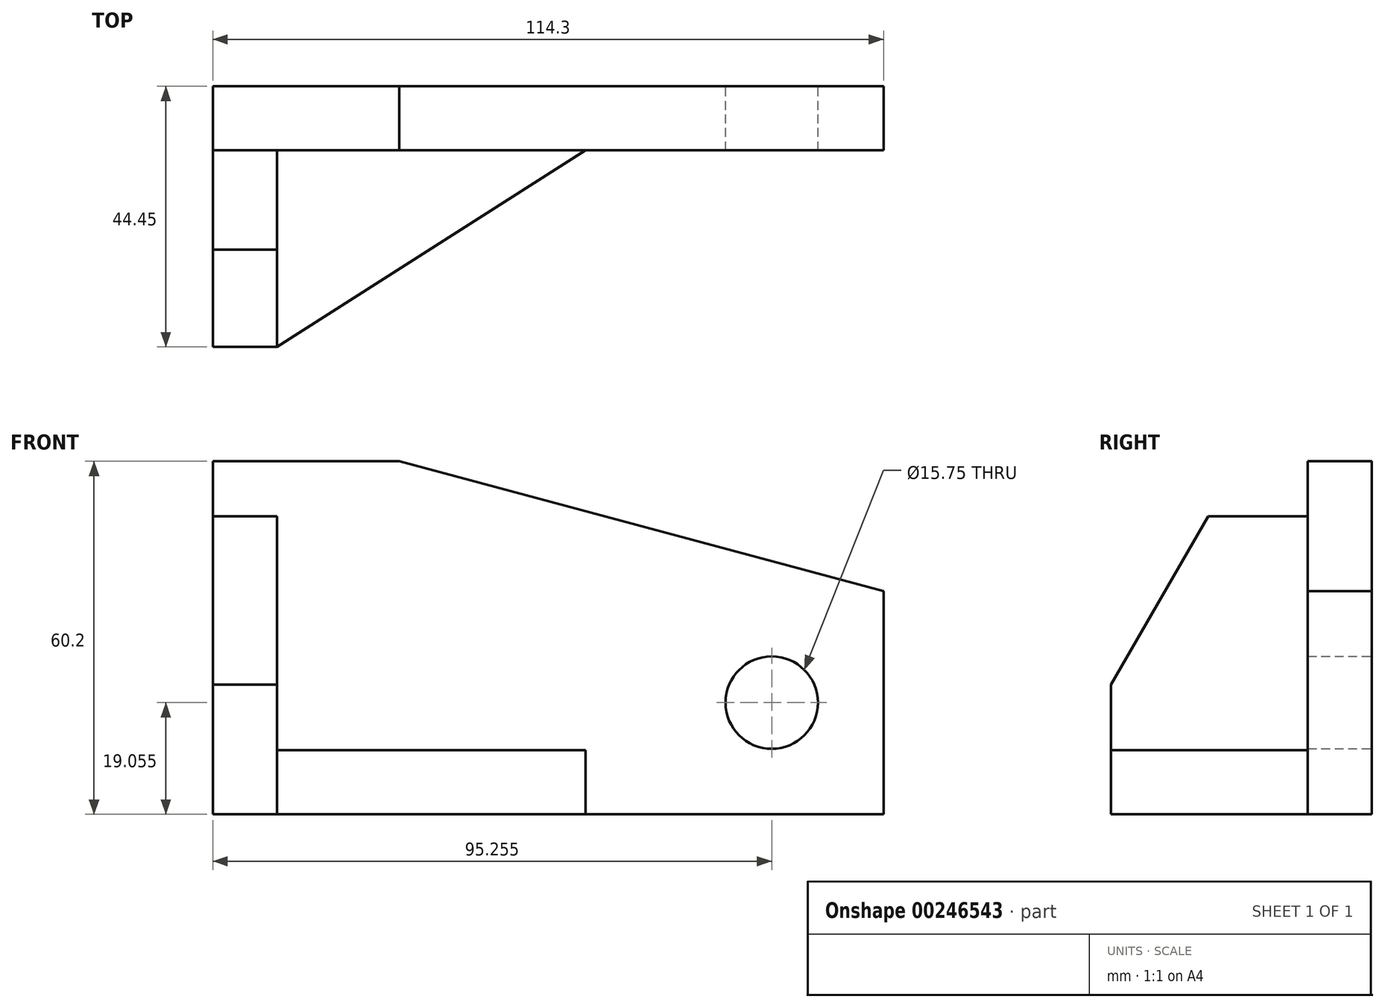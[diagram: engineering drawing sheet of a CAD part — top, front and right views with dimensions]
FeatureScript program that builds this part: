
annotation { "Feature Type Name" : "Feature", "Feature Type Description" : "" }
export const myFeature = defineFeature(function(context is Context, id is Id, definition is map)
    precondition{}
    {
        {
            var Q0;
            Q0=qCreatedBy(makeId("Front.planeOp"),FACE);
            var sketch = newSketch(context, id + "F0", { "sketchPlane" : qUnion([Q0])});
            skLineSegment(sketch, "E0.bottom", {"start": v(-52.56, 3.88) * mm, "end": v(-20.8, 3.88) * mm});
            skLineSegment(sketch, "E0.top", {"start": v(-52.56, -56.32) * mm, "end": v(61.74, -56.32) * mm});
            skLineSegment(sketch, "E0.left", {"start": v(-52.56, 3.88) * mm, "end": v(-52.56, -56.32) * mm});
            skLineSegment(sketch, "E0.right", {"start": v(61.74, -18.24) * mm, "end": v(61.74, -56.32) * mm});
            skLineSegment(sketch, "E1", {"start": v(-20.8, 3.88) * mm, "end": v(61.74, -18.24) * mm});
            skCircle(sketch, "E2", {"center": v(42.7, -37.27) * mm, "radius": 7.87 * mm});
            skSolve(sketch);
        }
        {
            var Q0;
            Q0=makeQuery(id+"F0.imprint","IMPRINT",FACE,{"disambiguationData":[TD([[makeQuery(id+"F0.imprint","IMPRINT",EDGE,{"derivedFrom":sQuery(id+"F0.wireOp",EDGE,"E0.top")}),1.0]])]});
            extrude(context, id + "F1", {"entities" : qUnion([Q0]), "depth" : 10.92 * mm});
        }
        {
            var Q0;
            Q0=makeQuery(id+"F1.opExtrude","CAP_FACE",FACE,{"disambiguationData":[OSD([sQuery(id+"F0.wireOp",EDGE,"E0.top"),sQuery(id+"F0.wireOp",EDGE,"E0.left"),sQuery(id+"F0.wireOp",EDGE,"E0.right"),sQuery(id+"F0.wireOp",EDGE,"E0.bottom"),sQuery(id+"F0.wireOp",EDGE,"E1"),sQuery(id+"F0.wireOp",EDGE,"E2")])],"isStart":false});
            var sketch = newSketch(context, id + "F2", { "sketchPlane" : qUnion([Q0])});
            skLineSegment(sketch, "E3", {"start": v(-52.56, -56.32) * mm, "end": v(-52.56, -5.52) * mm});
            skLineSegment(sketch, "E4", {"start": v(-52.56, -5.52) * mm, "end": v(-41.63, -5.52) * mm});
            skLineSegment(sketch, "E5", {"start": v(-41.63, -5.52) * mm, "end": v(-41.63, -56.32) * mm});
            skSolve(sketch);
        }
        {
            var Q0;
            {var subQ0=sQuery(id+"F2.wireOp",EDGE,"E3");Q0=makeQuery(id+"F2.imprint","IMPRINT",FACE,{"disambiguationData":[TD([[makeQuery(id+"F2.imprint","IMPRINT",EDGE,{"derivedFrom":subQ0}),1.0]])]});}
            extrude(context, id + "F3", {"entities" : qUnion([Q0]), "operationType" : NewBodyOperationType.ADD, "depth" : 33.53 * mm});
        }
        {
            var Q0;
            Q0=makeQuery(id+"F3.opExtrude","SWEPT_FACE",FACE,{"disambiguationData":[OSD([sQuery(id+"F2.wireOp",EDGE,"E5")])]});
            var sketch = newSketch(context, id + "F4", { "sketchPlane" : qUnion([Q0])});
            skLineSegment(sketch, "E6", {"start": v(-44.45, -56.32) * mm, "end": v(-44.45, -34.22) * mm});
            skLineSegment(sketch, "E7", {"start": v(-44.45, -34.22) * mm, "end": v(-27.88, -5.52) * mm});
            skLineSegment(sketch, "E8", {"start": v(-44.45, -56.32) * mm, "end": v(-44.45, -45.4) * mm});
            skLineSegment(sketch, "E9", {"start": v(-44.45, -45.4) * mm, "end": v(-10.92, -45.4) * mm});
            skLineSegment(sketch, "E10", {"start": v(-44.45, -34.22) * mm, "end": v(-44.45, -5.52) * mm});
            skLineSegment(sketch, "E11", {"start": v(-27.88, -5.52) * mm, "end": v(-10.92, -5.52) * mm});
            skSolve(sketch);
        }
        {
            var Q0;
            {var subQ0=sQuery(id+"F4.wireOp",EDGE,"E7");Q0=makeQuery(id+"F4.imprint","IMPRINT",FACE,{"disambiguationData":[TD([[makeQuery(id+"F4.imprint","IMPRINT",EDGE,{"derivedFrom":subQ0}),1.0]])]});}
            extrude(context, id + "F5", {"entities" : qUnion([Q0]), "operationType" : NewBodyOperationType.REMOVE, "oppositeDirection" : true, "depth" : 25.4 * mm});
        }
        {
            var Q0;
            Q0=makeQuery(id+"F3.opExtrude","SWEPT_FACE",FACE,{"disambiguationData":[OSD([sQuery(id+"F2.wireOp",EDGE,"E5")])]});
            var sketch = newSketch(context, id + "F6", { "sketchPlane" : qUnion([Q0])});
            skLineSegment(sketch, "E12", {"start": v(-44.45, -56.32) * mm, "end": v(-44.45, -45.4) * mm});
            skLineSegment(sketch, "E13", {"start": v(-44.45, -45.4) * mm, "end": v(-10.92, -45.4) * mm});
            skSolve(sketch);
        }
        {
            var Q0;
            Q0 = qSketchRegion(id + "F6", true);
            var Q1;
            Q1=makeQuery(id+"F6.imprint","IMPRINT",FACE,{"disambiguationData":[TD([[makeQuery(id+"F6.imprint","IMPRINT",EDGE,{"derivedFrom":sQuery(id+"F6.wireOp",EDGE,"E12")}),1.0]])]});
            extrude(context, id + "F7", {"entities" : qUnion([Q0, Q1]), "operationType" : NewBodyOperationType.ADD, "depth" : 52.58 * mm});
        }
        {
            var Q0;
            Q0=makeQuery(id+"F7.opExtrude","SWEPT_FACE",FACE,{"disambiguationData":[OSD([sQuery(id+"F6.wireOp",EDGE,"E13")])]});
            var sketch = newSketch(context, id + "F8", { "sketchPlane" : qUnion([Q0])});
            skLineSegment(sketch, "E14", {"start": v(-41.63, -44.45) * mm, "end": v(10.94, -10.92) * mm});
            skSolve(sketch);
        }
        {
            var Q0;
            Q0 = qSketchRegion(id + "F8", true);
            var Q1;
            Q1=makeQuery(id+"F8.imprint","IMPRINT",FACE,{"disambiguationData":[TD([[makeQuery(id+"F8.imprint","IMPRINT",EDGE,{"derivedFrom":sQuery(id+"F8.wireOp",EDGE,"E14")}),-1.0]])]});
            extrude(context, id + "F9", {"entities" : qUnion([Q0, Q1]), "operationType" : NewBodyOperationType.REMOVE, "oppositeDirection" : true, "depth" : 25.4 * mm});
        }
    });
